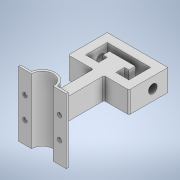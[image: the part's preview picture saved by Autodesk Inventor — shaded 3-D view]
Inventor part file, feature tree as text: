
AUTODESK INVENTOR PART (.ipt)
format: ipt  version: 2022 (Build 260153000, 153)  size: 226,816 bytes
history: native  units: mm
features: extrude x6, sketch x6, plane x1, fillet x1, thread x1
ambient origin geometry x8: Origin, YZ Plane, XZ Plane, XY Plane, X Axis, Y Axis, Z Axis, Center Point
bodies: Solid1 (feature_tree)
feature tree (15):
  extrude  "Extrusion1"  Depth=60.0mm
  plane  "Work Plane1"
  extrude  "Extrusion2"  Depth=5.0mm
  sketch  "Sketch5"  dims[d5=5.0mm d6=12.5mm]
  extrude  "Extrusion4"  Depth=5.0mm
  extrude  "Extrusion5"  Depth=150.0mm
  extrude  "Extrusion6"  Depth=60.0mm
  fillet  "Fillet2"  Radius=10.0mm
  extrude  "Extrusion7"  Depth=20.0mm
  thread  "Thread1"  [1 undecoded]
  sketch  "Sketch1"  dims[d0=50.0mm d1=60.0mm]
  sketch  "Sketch3"  dims[d2=30.0mm d3=5.0mm]
  sketch  "Sketch6"  dims[d7=300.0mm d8=150.0mm]
  sketch  "Sketch7"  dims[d9=80.0mm d10=60.0mm d11=10.0mm]
  sketch  "Sketch8"  dims[d12=10.0mm d13=20.0mm d14=10.0mm d15=10.0mm d16=15.0mm d17=150.0mm d18=0.0mm d21=30.0mm d35=50.0mm d36=0.0mm d38=20.0mm d41=20.0mm d42=0.0mm d43=50.0mm d44=50.0mm d45=10.0mm d46=10.0mm d47=10.0mm d48=0.0mm d49=50.0mm d50=50.0mm d51=10.0mm d52=10.0mm d53=10.0mm d54=0.0mm d62=50.0mm d63=10.0mm d64=3.0mm d65=20.0mm d66=20.0mm d67=20.0mm d68=0.0mm d69=20.0mm d70=0.0mm]
note: 1 required parameter value undecoded (feature->parameter linkage not recoverable at this tier; creation-order binding heuristic only, values carry confidence <= 0.55)
